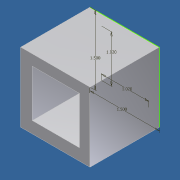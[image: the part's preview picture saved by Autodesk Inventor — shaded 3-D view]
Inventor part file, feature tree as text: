
AUTODESK INVENTOR PART (.ipt)
format: ipt  version: unknown  size: 166,912 bytes
history: native  units: in
note: dims shown in document units (in); Inventor stores cm internally (conversion verified against a paired STEP export)
features: extrude x1, sketch x1
ambient origin geometry x8: Origin, YZ Plane, XZ Plane, XY Plane, X Axis, Y Axis, Z Axis, Center Point
bodies: Solid1 (feature_tree)
feature tree (2):
  extrude  "Extrusion1"  Depth=1.02in
  sketch  "Sketch1"  dims[d0=1.02in d1=1.02in d4=1.5in d5=1.5in d6=1.5in d7=0.0in]
